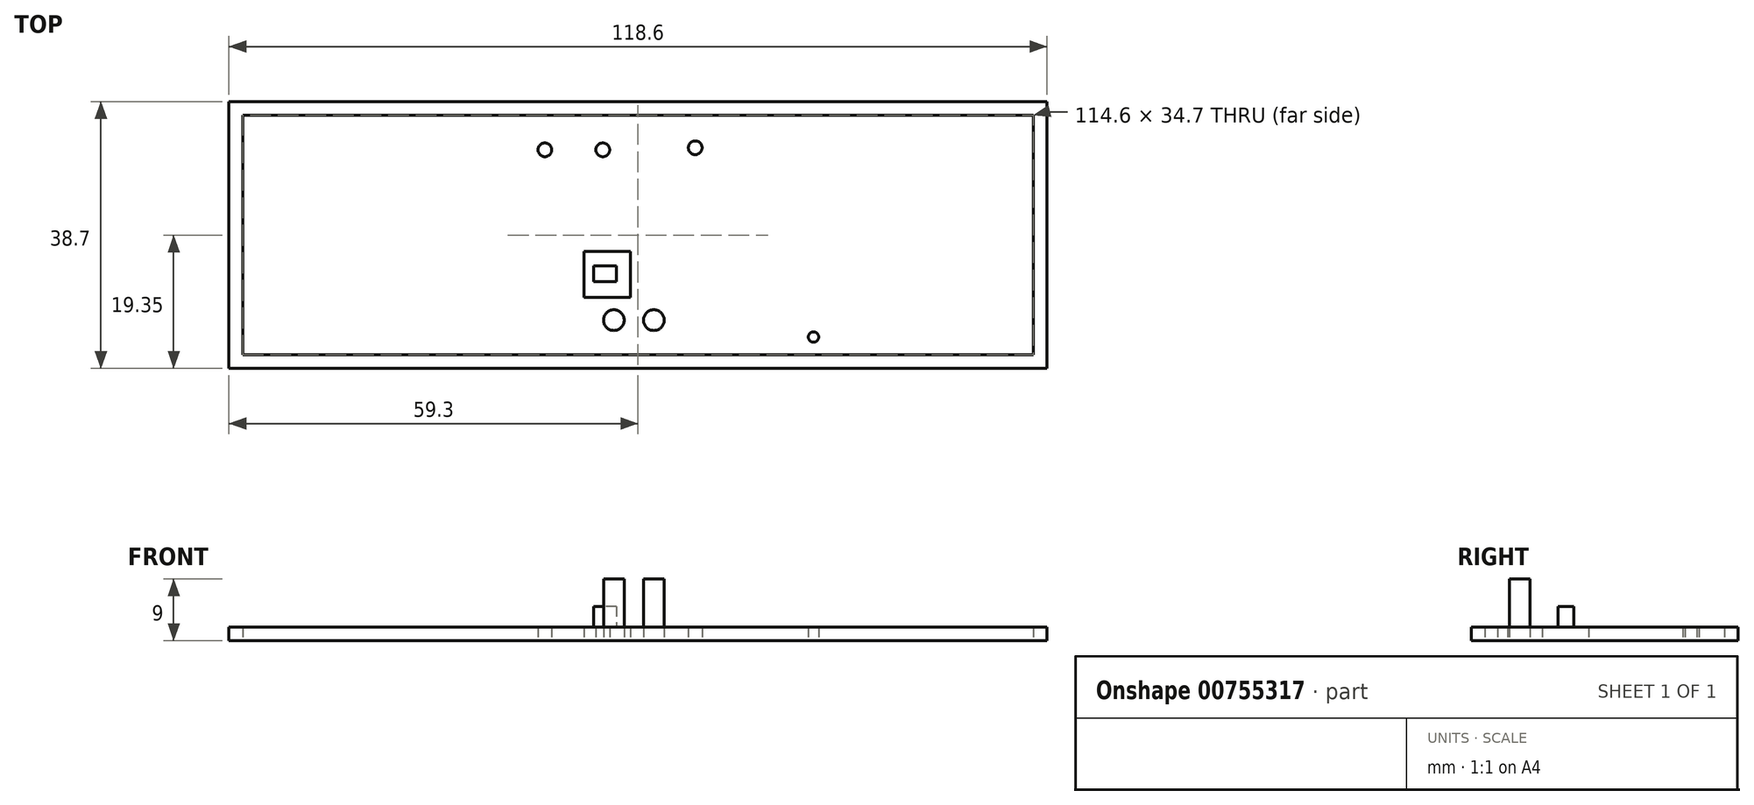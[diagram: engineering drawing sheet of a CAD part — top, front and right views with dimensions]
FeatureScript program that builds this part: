
annotation { "Feature Type Name" : "Feature", "Feature Type Description" : "" }
export const myFeature = defineFeature(function(context is Context, id is Id, definition is map)
    precondition{}
    {
        {
            var Q0;
            Q0=qCreatedBy(makeId("Top.planeOp"),FACE);
            var sketch = newSketch(context, id + "F0", { "sketchPlane" : qUnion([Q0])});
            skLineSegment(sketch, "E0.bottom", {"start": v(59.3, -19.35) * mm, "end": v(-59.3, -19.35) * mm});
            skLineSegment(sketch, "E0.top", {"start": v(59.3, 19.35) * mm, "end": v(-59.3, 19.35) * mm});
            skLineSegment(sketch, "E0.left", {"start": v(59.3, -19.35) * mm, "end": v(59.3, 19.35) * mm});
            skLineSegment(sketch, "E0.right", {"start": v(-59.3, -19.35) * mm, "end": v(-59.3, 19.35) * mm});
            skPoint(sketch, "E0.middle", {"position": v(0, 0) * mm});
            skText(sketch, "E1", { "text": "zuid", "fontName": "OpenSans-Regular.ttf"});
            skLineSegment(sketch, "E2.bottom", {"start": v(-7.8, -2.35) * mm, "end": v(-1.1, -2.35) * mm});
            skLineSegment(sketch, "E2.top", {"start": v(-7.8, -9.05) * mm, "end": v(-1.1, -9.05) * mm});
            skLineSegment(sketch, "E2.left", {"start": v(-7.8, -2.35) * mm, "end": v(-7.8, -9.05) * mm});
            skLineSegment(sketch, "E2.right", {"start": v(-1.1, -2.35) * mm, "end": v(-1.1, -9.05) * mm});
            skCircle(sketch, "E3", {"center": v(-13.5, 12.35) * mm, "radius": 1 * mm});
            skCircle(sketch, "E4", {"center": v(-5.1, 12.35) * mm, "radius": 1 * mm});
            skCircle(sketch, "E5", {"center": v(8.3, 12.65) * mm, "radius": 1 * mm});
            skCircle(sketch, "E6", {"center": v(-3.5, -12.35) * mm, "radius": 1.5 * mm});
            skCircle(sketch, "E7", {"center": v(2.3, -12.35) * mm, "radius": 1.5 * mm});
            skCircle(sketch, "E8", {"center": v(25.45, -14.8) * mm, "radius": 0.75 * mm});
            skLineSegment(sketch, "E9.bottom", {"start": v(57.3, -17.35) * mm, "end": v(-57.3, -17.35) * mm});
            skLineSegment(sketch, "E9.top", {"start": v(57.3, 17.35) * mm, "end": v(-57.3, 17.35) * mm});
            skLineSegment(sketch, "E9.left", {"start": v(57.3, -17.35) * mm, "end": v(57.3, 17.35) * mm});
            skLineSegment(sketch, "E9.right", {"start": v(-57.3, -17.35) * mm, "end": v(-57.3, 17.35) * mm});
            skLineSegment(sketch, "E10.bottom", {"start": v(-3.14, -6.75) * mm, "end": v(-6.4, -6.75) * mm});
            skLineSegment(sketch, "E10.top", {"start": v(-3.14, -4.47) * mm, "end": v(-6.4, -4.47) * mm});
            skLineSegment(sketch, "E10.left", {"start": v(-3.14, -6.75) * mm, "end": v(-3.14, -4.47) * mm});
            skLineSegment(sketch, "E10.right", {"start": v(-6.4, -6.75) * mm, "end": v(-6.4, -4.47) * mm});
            skPoint(sketch, "E10.middle", {"position": v(-4.77, -5.6) * mm});
            const initialGuessF0  = {"E1": [-0.00456, -0.07513, 1, 0, 0.00625]};
            skSetInitialGuess(sketch, initialGuessF0);
            skSolve(sketch);
        }
        {
            var Q0;
            Q0=makeQuery(id+"F0.imprint","IMPRINT",FACE,{"disambiguationData":[TD([[makeQuery(id+"F0.imprint","IMPRINT",EDGE,{"derivedFrom":sQuery(id+"F0.wireOp",EDGE,"E0.bottom")}),-1.0]])]});
            var Q1;
            Q1=makeQuery(id+"F0.imprint","IMPRINT",FACE,{"disambiguationData":[TD([[makeQuery(id+"F0.imprint","IMPRINT",EDGE,{"derivedFrom":sQuery(id+"F0.wireOp",EDGE,"E2.bottom")}),-1.0]])]});
            var Q2;
            Q2=makeQuery(id+"F0.imprint","IMPRINT",FACE,{"disambiguationData":[TD([[makeQuery(id+"F0.imprint","IMPRINT",EDGE,{"derivedFrom":sQuery(id+"F0.wireOp",EDGE,"E3")}),1.0]])]});
            var Q3;
            Q3=makeQuery(id+"F0.imprint","IMPRINT",FACE,{"disambiguationData":[TD([[makeQuery(id+"F0.imprint","IMPRINT",EDGE,{"derivedFrom":sQuery(id+"F0.wireOp",EDGE,"E4")}),1.0]])]});
            var Q4;
            Q4=makeQuery(id+"F0.imprint","IMPRINT",FACE,{"disambiguationData":[TD([[makeQuery(id+"F0.imprint","IMPRINT",EDGE,{"derivedFrom":sQuery(id+"F0.wireOp",EDGE,"E5")}),1.0]])]});
            var Q5;
            Q5=makeQuery(id+"F0.imprint","IMPRINT",FACE,{"disambiguationData":[TD([[makeQuery(id+"F0.imprint","IMPRINT",EDGE,{"derivedFrom":sQuery(id+"F0.wireOp",EDGE,"E8")}),1.0]])]});
            extrude(context, id + "F1", {"entities" : qUnion([Q0, Q1, Q2, Q3, Q4, Q5]), "depth" : 2 * mm, "offsetDistance" : 25 * mm});
        }
        {
            var Q0;
            Q0=makeQuery(id+"F0.imprint","IMPRINT",FACE,{"disambiguationData":[TD([[makeQuery(id+"F0.imprint","IMPRINT",EDGE,{"derivedFrom":sQuery(id+"F0.wireOp",EDGE,"E6")}),1.0]])]});
            var Q1;
            Q1=makeQuery(id+"F0.imprint","IMPRINT",FACE,{"disambiguationData":[TD([[makeQuery(id+"F0.imprint","IMPRINT",EDGE,{"derivedFrom":sQuery(id+"F0.wireOp",EDGE,"E7")}),1.0]])]});
            extrude(context, id + "F2", {"entities" : qUnion([Q0, Q1]), "depth" : 9 * mm, "offsetDistance" : 25 * mm});
        }
        {
            var Q0;
            Q0=makeQuery(id+"F0.imprint","IMPRINT",FACE,{"disambiguationData":[TD([[makeQuery(id+"F0.imprint","IMPRINT",EDGE,{"derivedFrom":sQuery(id+"F0.wireOp",EDGE,"E10.bottom")}),-1.0]])]});
            extrude(context, id + "F3", {"entities" : qUnion([Q0]), "operationType" : NewBodyOperationType.ADD, "depth" : 5 * mm, "offsetDistance" : 25 * mm});
        }
    });
